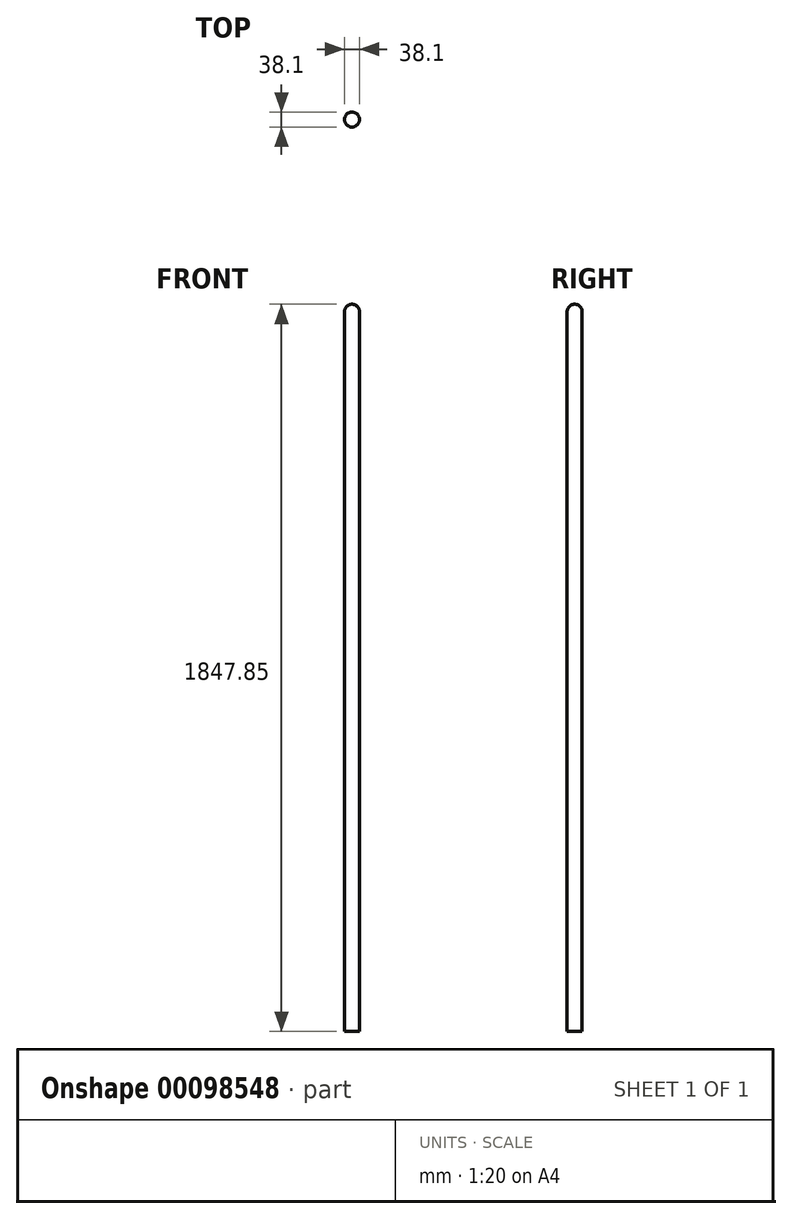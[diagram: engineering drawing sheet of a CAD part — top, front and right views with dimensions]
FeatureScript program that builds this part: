
annotation { "Feature Type Name" : "Feature", "Feature Type Description" : "" }
export const myFeature = defineFeature(function(context is Context, id is Id, definition is map)
    precondition{}
    {
        {
            var Q0;
            Q0=qCreatedBy(makeId("Front.planeOp"),FACE);
            var sketch = newSketch(context, id + "F0", { "sketchPlane" : qUnion([Q0])});
            skLineSegment(sketch, "E0.bottom", {"start": v(0, 914.4) * mm, "end": v(19.05, 914.4) * mm, "construction": true});
            skLineSegment(sketch, "E0.top", {"start": v(0, -914.4) * mm, "end": v(19.05, -914.4) * mm});
            skLineSegment(sketch, "E0.left", {"start": v(0, 914.4) * mm, "end": v(0, -914.4) * mm});
            skLineSegment(sketch, "E0.right", {"start": v(19.05, 914.4) * mm, "end": v(19.05, -914.4) * mm});
            skLineSegment(sketch, "E1", {"start": v(0, 914.4) * mm, "end": v(0, 933.45) * mm});
            skArc(sketch, "E2", {"start": v(19.05, 914.4) * mm, "mid": v(13.47, 927.87) * mm, "end": v(0, 933.45) * mm});
            skSolve(sketch);
        }
        {
            var Q0;
            Q0 = qSketchRegion(id + "F0", true);
            var Q1;
            Q1=sQuery(id+"F0.wireOp",EDGE,"E0.left");
            revolve(context, id + "F1", {"entities" : qUnion([Q0]), "axis" : qUnion([Q1]), "revolveType" : RevolveType.FULL});
        }
    });
